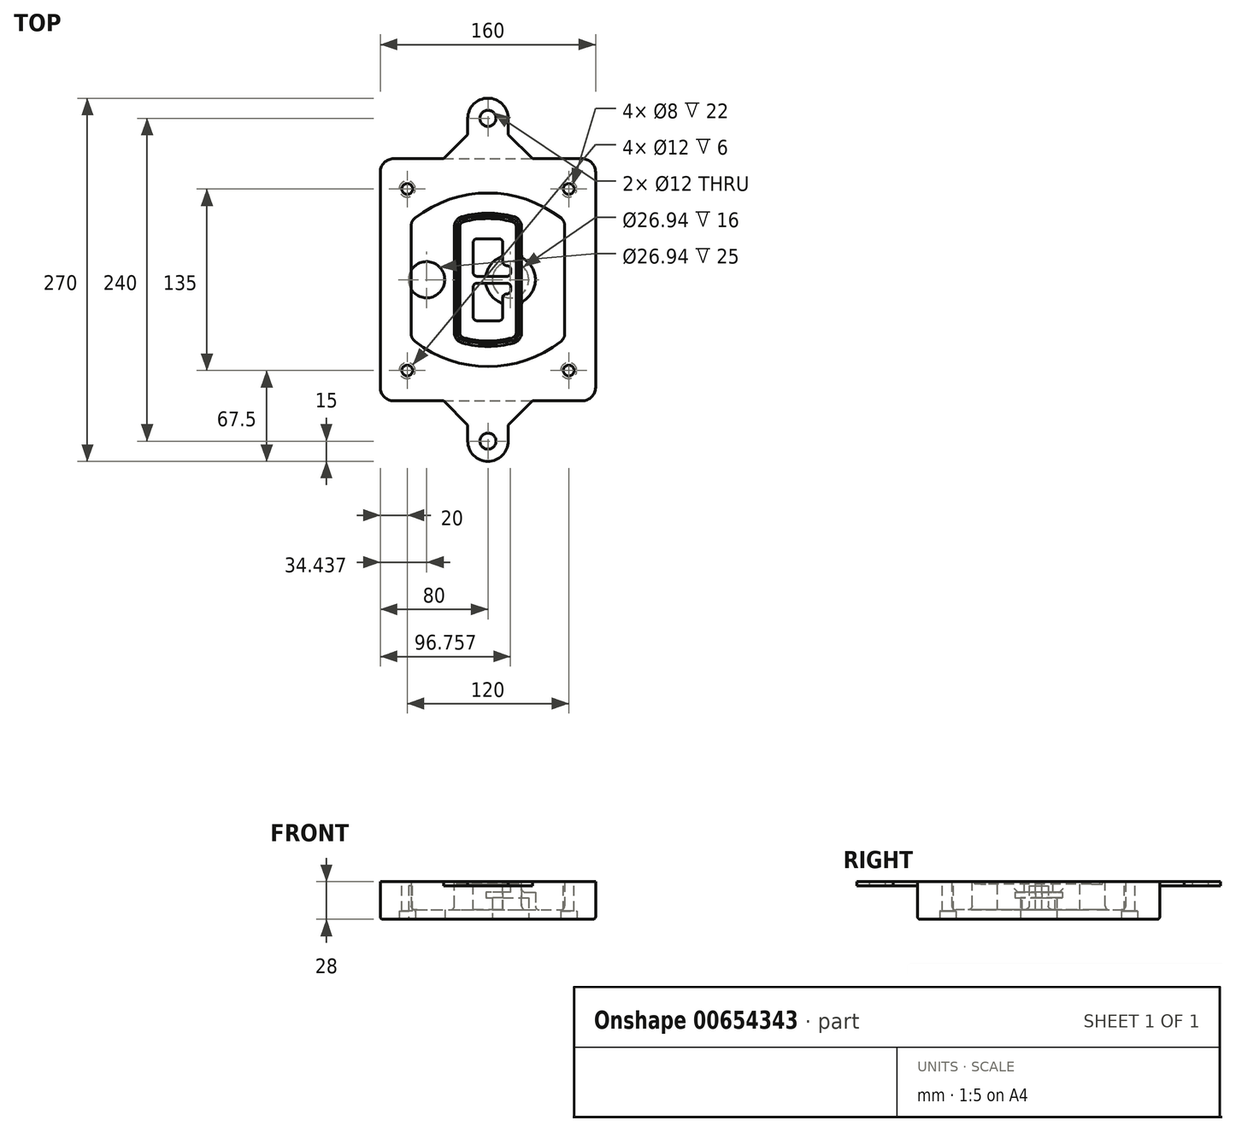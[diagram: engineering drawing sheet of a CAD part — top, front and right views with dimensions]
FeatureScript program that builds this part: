
annotation { "Feature Type Name" : "Feature", "Feature Type Description" : "" }
export const myFeature = defineFeature(function(context is Context, id is Id, definition is map)
    precondition{}
    {
        {
            var Q0;
            Q0=qCreatedBy(makeId("Top.planeOp"),FACE);
            var sketch = newSketch(context, id + "F0", { "sketchPlane" : qUnion([Q0])});
            skPoint(sketch, "E0.rect.middle", {"position": v(0, 0) * mm});
            skLineSegment(sketch, "E1.bottom", {"start": v(-70, -90) * mm, "end": v(70, -90) * mm});
            skLineSegment(sketch, "E1.top", {"start": v(-70, 90) * mm, "end": v(70, 90) * mm});
            skLineSegment(sketch, "E1.left", {"start": v(-80, -80) * mm, "end": v(-80, 80) * mm});
            skLineSegment(sketch, "E1.right", {"start": v(80, -80) * mm, "end": v(80, 80) * mm});
            skLineSegment(sketch, "E2", {"start": v(-80, 90) * mm, "end": v(80, -90) * mm, "construction": true});
            skLineSegment(sketch, "E3", {"start": v(80, 90) * mm, "end": v(-80, -90) * mm, "construction": true});
            skCircle(sketch, "E4", {"center": v(-60, 67.5) * mm, "radius": 4 * mm});
            skCircle(sketch, "E5", {"center": v(60, 67.5) * mm, "radius": 4 * mm});
            skCircle(sketch, "E6", {"center": v(60, -67.5) * mm, "radius": 4 * mm});
            skCircle(sketch, "E7", {"center": v(-60, -67.5) * mm, "radius": 4 * mm});
            skLineSegment(sketch, "E8", {"start": v(-60, 67.5) * mm, "end": v(60, 67.5) * mm, "construction": true});
            skLineSegment(sketch, "E9", {"start": v(60, 67.5) * mm, "end": v(60, -67.5) * mm, "construction": true});
            skLineSegment(sketch, "E10", {"start": v(60, -67.5) * mm, "end": v(-60, -67.5) * mm, "construction": true});
            skLineSegment(sketch, "E11", {"start": v(-60, -67.5) * mm, "end": v(-60, 67.5) * mm, "construction": true});
            skLineSegment(sketch, "E12", {"start": v(-60, 40.3) * mm, "end": v(-60, -40.3) * mm});
            skLineSegment(sketch, "E13", {"start": v(60, 40.3) * mm, "end": v(60, -40.3) * mm});
            skArc(sketch, "E14", {"start": v(56.15, 48.18) * mm, "mid": v(0, 67.5) * mm, "end": v(-56.15, 48.18) * mm});
            skArc(sketch, "E15", {"start": v(-56.15, -48.18) * mm, "mid": v(0, -67.5) * mm, "end": v(56.15, -48.18) * mm});
            skLineSegment(sketch, "E16", {"start": v(-60, 0) * mm, "end": v(60, 0) * mm, "construction": true});
            skPoint(sketch, "E17.visualSharp", {"position": v(-60, -45) * mm});
            skArc(sketch, "E17.filletArc", {"start": v(-60, -40.3) * mm, "mid": v(-58.99, -44.68) * mm, "end": v(-56.15, -48.18) * mm});
            skPoint(sketch, "E18.visualSharp", {"position": v(-60, 45) * mm});
            skArc(sketch, "E18.filletArc", {"start": v(-56.15, 48.18) * mm, "mid": v(-58.99, 44.68) * mm, "end": v(-60, 40.3) * mm});
            skPoint(sketch, "E19.visualSharp", {"position": v(60, 45) * mm});
            skArc(sketch, "E19.filletArc", {"start": v(60, 40.3) * mm, "mid": v(58.99, 44.68) * mm, "end": v(56.15, 48.18) * mm});
            skPoint(sketch, "E20.visualSharp", {"position": v(60, -45) * mm});
            skArc(sketch, "E20.filletArc", {"start": v(56.15, -48.18) * mm, "mid": v(58.99, -44.68) * mm, "end": v(60, -40.3) * mm});
            skPoint(sketch, "E21.visualSharp", {"position": v(-80, 90) * mm});
            skArc(sketch, "E21.filletArc", {"start": v(-70, 90) * mm, "mid": v(-77.07, 87.07) * mm, "end": v(-80, 80) * mm});
            skPoint(sketch, "E22.visualSharp", {"position": v(80, 90) * mm});
            skArc(sketch, "E22.filletArc", {"start": v(80, 80) * mm, "mid": v(77.07, 87.07) * mm, "end": v(70, 90) * mm});
            skPoint(sketch, "E23.visualSharp", {"position": v(80, -90) * mm});
            skArc(sketch, "E23.filletArc", {"start": v(70, -90) * mm, "mid": v(77.07, -87.07) * mm, "end": v(80, -80) * mm});
            skPoint(sketch, "E24.visualSharp", {"position": v(-80, -90) * mm});
            skArc(sketch, "E24.filletArc", {"start": v(-80, -80) * mm, "mid": v(-77.07, -87.07) * mm, "end": v(-70, -90) * mm});
            skArc(sketch, "E25.0", {"start": v(57, 40.3) * mm, "mid": v(56.3, 43.36) * mm, "end": v(54.3, 45.81) * mm});
            skLineSegment(sketch, "E25.1", {"start": v(57, 40.3) * mm, "end": v(57, -40.3) * mm});
            skArc(sketch, "E25.2", {"start": v(54.3, -45.81) * mm, "mid": v(56.3, -43.36) * mm, "end": v(57, -40.3) * mm});
            skArc(sketch, "E25.3", {"start": v(-54.3, -45.81) * mm, "mid": v(0, -64.5) * mm, "end": v(54.3, -45.81) * mm});
            skArc(sketch, "E25.4", {"start": v(-57, -40.3) * mm, "mid": v(-56.3, -43.36) * mm, "end": v(-54.3, -45.81) * mm});
            skArc(sketch, "E25.5", {"start": v(54.3, 45.81) * mm, "mid": v(0, 64.5) * mm, "end": v(-54.3, 45.81) * mm});
            skLineSegment(sketch, "E25.6", {"start": v(-57, 40.3) * mm, "end": v(-57, -40.3) * mm});
            skArc(sketch, "E25.7", {"start": v(-54.3, 45.81) * mm, "mid": v(-56.3, 43.36) * mm, "end": v(-57, 40.3) * mm});
            skArc(sketch, "E26.0", {"start": v(-58.62, 51.33) * mm, "mid": v(-62.58, 46.43) * mm, "end": v(-64, 40.3) * mm});
            skArc(sketch, "E26.1", {"start": v(58.62, 51.33) * mm, "mid": v(0, 71.5) * mm, "end": v(-58.62, 51.33) * mm});
            skArc(sketch, "E26.2", {"start": v(64, 40.3) * mm, "mid": v(62.58, 46.43) * mm, "end": v(58.62, 51.33) * mm});
            skLineSegment(sketch, "E26.3", {"start": v(64, 40.3) * mm, "end": v(64, -40.3) * mm});
            skArc(sketch, "E26.4", {"start": v(58.62, -51.33) * mm, "mid": v(62.58, -46.43) * mm, "end": v(64, -40.3) * mm});
            skLineSegment(sketch, "E26.5", {"start": v(-64, 40.3) * mm, "end": v(-64, -40.3) * mm});
            skArc(sketch, "E26.6", {"start": v(-58.62, -51.33) * mm, "mid": v(0, -71.5) * mm, "end": v(58.62, -51.33) * mm});
            skArc(sketch, "E26.7", {"start": v(-64, -40.3) * mm, "mid": v(-62.58, -46.43) * mm, "end": v(-58.62, -51.33) * mm});
            skSolve(sketch);
        }
        {
            var Q0;
            Q0=makeQuery(id+"F0.imprint","IMPRINT",FACE,{"disambiguationData":[TD([[makeQuery(id+"F0.imprint","IMPRINT",EDGE,{"derivedFrom":sQuery(id+"F0.wireOp",EDGE,"E1.bottom")}),1.0]])]});
            var Q1;
            Q1=makeQuery(id+"F0.imprint","IMPRINT",FACE,{"disambiguationData":[TD([[makeQuery(id+"F0.imprint","IMPRINT",EDGE,{"derivedFrom":sQuery(id+"F0.wireOp",EDGE,"E12")}),1.0]])]});
            var Q2;
            Q2=makeQuery(id+"F0.imprint","IMPRINT",FACE,{"disambiguationData":[TD([[makeQuery(id+"F0.imprint","IMPRINT",EDGE,{"derivedFrom":sQuery(id+"F0.wireOp",EDGE,"E25.0")}),1.0]])]});
            var Q3;
            Q3=makeQuery(id+"F0.imprint","IMPRINT",FACE,{"disambiguationData":[TD([[makeQuery(id+"F0.imprint","IMPRINT",EDGE,{"derivedFrom":sQuery(id+"F0.wireOp",EDGE,"E12")}),-1.0]])]});
            extrude(context, id + "F1", {"entities" : qUnion([Q0, Q1, Q2, Q3]), "oppositeDirection" : true, "depth" : 25 * mm});
        }
        {
            var Q0;
            Q0=makeQuery(id+"F0.imprint","IMPRINT",FACE,{"disambiguationData":[TD([[makeQuery(id+"F0.imprint","IMPRINT",EDGE,{"derivedFrom":sQuery(id+"F0.wireOp",EDGE,"E12")}),1.0]])]});
            extrude(context, id + "F2", {"entities" : qUnion([Q0]), "operationType" : NewBodyOperationType.ADD, "depth" : 3 * mm});
        }
        {
            var Q0;
            Q0=makeQuery(id+"F0.imprint","IMPRINT",FACE,{"disambiguationData":[TD([[makeQuery(id+"F0.imprint","IMPRINT",EDGE,{"derivedFrom":sQuery(id+"F0.wireOp",EDGE,"E25.0")}),1.0]])]});
            extrude(context, id + "F3", {"entities" : qUnion([Q0]), "operationType" : NewBodyOperationType.REMOVE, "oppositeDirection" : true, "depth" : 18 * mm});
        }
        {
            var Q0;
            Q0=makeQuery(id+"F2.opExtrude","CAP_FACE",FACE,{"disambiguationData":[OSD([sQuery(id+"F0.wireOp",EDGE,"E12"),sQuery(id+"F0.wireOp",EDGE,"E13"),sQuery(id+"F0.wireOp",EDGE,"E14"),sQuery(id+"F0.wireOp",EDGE,"E15"),sQuery(id+"F0.wireOp",EDGE,"E17.filletArc"),sQuery(id+"F0.wireOp",EDGE,"E18.filletArc"),sQuery(id+"F0.wireOp",EDGE,"E19.filletArc"),sQuery(id+"F0.wireOp",EDGE,"E20.filletArc"),sQuery(id+"F0.wireOp",EDGE,"E25.0"),sQuery(id+"F0.wireOp",EDGE,"E25.1"),sQuery(id+"F0.wireOp",EDGE,"E25.2"),sQuery(id+"F0.wireOp",EDGE,"E25.3"),sQuery(id+"F0.wireOp",EDGE,"E25.4"),sQuery(id+"F0.wireOp",EDGE,"E25.5"),sQuery(id+"F0.wireOp",EDGE,"E25.6"),sQuery(id+"F0.wireOp",EDGE,"E25.7")])],"isStart":false});
            var sketch = newSketch(context, id + "F4", { "sketchPlane" : qUnion([Q0])});
            skArc(sketch, "E27.0", {"start": v(-19.08, -46.97) * mm, "mid": v(0, -49.5) * mm, "end": v(19.08, -46.97) * mm});
            skArc(sketch, "E28.0", {"start": v(19.08, 46.97) * mm, "mid": v(0, 49.5) * mm, "end": v(-19.08, 46.97) * mm});
            skLineSegment(sketch, "E29", {"start": v(-25, 39.25) * mm, "end": v(-25, -39.25) * mm});
            skLineSegment(sketch, "E30", {"start": v(25, 39.25) * mm, "end": v(25, -39.25) * mm});
            skLineSegment(sketch, "E31", {"start": v(-25, 45.1) * mm, "end": v(25, 45.1) * mm, "construction": true});
            skLineSegment(sketch, "E32", {"start": v(-25, -45.1) * mm, "end": v(25, -45.1) * mm, "construction": true});
            skPoint(sketch, "E33.visualSharp", {"position": v(-25, 45.1) * mm});
            skArc(sketch, "E33.filletArc", {"start": v(-19.08, 46.97) * mm, "mid": v(-23.35, 44.11) * mm, "end": v(-25, 39.25) * mm});
            skPoint(sketch, "E34.visualSharp", {"position": v(25, 45.1) * mm});
            skArc(sketch, "E34.filletArc", {"start": v(25, 39.25) * mm, "mid": v(23.35, 44.11) * mm, "end": v(19.08, 46.97) * mm});
            skPoint(sketch, "E35.visualSharp", {"position": v(25, -45.1) * mm});
            skArc(sketch, "E35.filletArc", {"start": v(19.08, -46.97) * mm, "mid": v(23.35, -44.11) * mm, "end": v(25, -39.25) * mm});
            skPoint(sketch, "E36.visualSharp", {"position": v(-25, -45.1) * mm});
            skArc(sketch, "E36.filletArc", {"start": v(-25, -39.25) * mm, "mid": v(-23.35, -44.11) * mm, "end": v(-19.08, -46.97) * mm});
            skArc(sketch, "E37.0", {"start": v(54.3, 45.81) * mm, "mid": v(0, 64.5) * mm, "end": v(-54.3, 45.81) * mm});
            skArc(sketch, "E37.1", {"start": v(-54.3, 45.81) * mm, "mid": v(-56.3, 43.36) * mm, "end": v(-57, 40.3) * mm});
            skLineSegment(sketch, "E37.2", {"start": v(-57, 40.3) * mm, "end": v(-57, -40.3) * mm});
            skArc(sketch, "E37.3", {"start": v(-57, -40.3) * mm, "mid": v(-56.3, -43.36) * mm, "end": v(-54.3, -45.81) * mm});
            skArc(sketch, "E37.4", {"start": v(-54.3, -45.81) * mm, "mid": v(0, -64.5) * mm, "end": v(54.3, -45.81) * mm});
            skArc(sketch, "E37.5", {"start": v(54.3, -45.81) * mm, "mid": v(56.3, -43.36) * mm, "end": v(57, -40.3) * mm});
            skLineSegment(sketch, "E37.6", {"start": v(57, 40.3) * mm, "end": v(57, -40.3) * mm});
            skArc(sketch, "E37.7", {"start": v(57, 40.3) * mm, "mid": v(56.3, 43.36) * mm, "end": v(54.3, 45.81) * mm});
            skLineSegment(sketch, "E38.0", {"start": v(23, 39.25) * mm, "end": v(23, -39.25) * mm});
            skArc(sketch, "E38.1", {"start": v(18.56, -45.04) * mm, "mid": v(21.76, -42.9) * mm, "end": v(23, -39.25) * mm});
            skArc(sketch, "E38.2", {"start": v(-18.56, -45.04) * mm, "mid": v(0, -47.5) * mm, "end": v(18.56, -45.04) * mm});
            skArc(sketch, "E38.3", {"start": v(-23, -39.25) * mm, "mid": v(-21.76, -42.9) * mm, "end": v(-18.56, -45.04) * mm});
            skLineSegment(sketch, "E38.4", {"start": v(-23, 39.25) * mm, "end": v(-23, -39.25) * mm});
            skArc(sketch, "E38.5", {"start": v(23, 39.25) * mm, "mid": v(21.76, 42.9) * mm, "end": v(18.56, 45.04) * mm});
            skArc(sketch, "E38.6", {"start": v(-18.56, 45.04) * mm, "mid": v(-21.76, 42.9) * mm, "end": v(-23, 39.25) * mm});
            skArc(sketch, "E38.7", {"start": v(18.56, 45.04) * mm, "mid": v(0, 47.5) * mm, "end": v(-18.56, 45.04) * mm});
            skArc(sketch, "E39.0", {"start": v(21, 39.25) * mm, "mid": v(20.18, 41.68) * mm, "end": v(18.04, 43.1) * mm});
            skLineSegment(sketch, "E39.1", {"start": v(21, 39.25) * mm, "end": v(21, -39.25) * mm});
            skArc(sketch, "E39.2", {"start": v(18.04, -43.1) * mm, "mid": v(20.18, -41.68) * mm, "end": v(21, -39.25) * mm});
            skArc(sketch, "E39.3", {"start": v(-18.04, -43.1) * mm, "mid": v(0, -45.5) * mm, "end": v(18.04, -43.1) * mm});
            skArc(sketch, "E39.4", {"start": v(-21, -39.25) * mm, "mid": v(-20.18, -41.68) * mm, "end": v(-18.04, -43.1) * mm});
            skArc(sketch, "E39.5", {"start": v(18.04, 43.1) * mm, "mid": v(0, 45.5) * mm, "end": v(-18.04, 43.1) * mm});
            skLineSegment(sketch, "E39.6", {"start": v(-21, 39.25) * mm, "end": v(-21, -39.25) * mm});
            skArc(sketch, "E39.7", {"start": v(-18.04, 43.1) * mm, "mid": v(-20.18, 41.68) * mm, "end": v(-21, 39.25) * mm});
            skLineSegment(sketch, "E40", {"start": v(-25, 0) * mm, "end": v(25, 0) * mm, "construction": true});
            skLineSegment(sketch, "E41", {"start": v(-11, 5.5) * mm, "end": v(-11, 27.5) * mm});
            skLineSegment(sketch, "E42", {"start": v(-8, 30.5) * mm, "end": v(8, 30.5) * mm});
            skLineSegment(sketch, "E43", {"start": v(11, 27.5) * mm, "end": v(11, 13.5) * mm});
            skLineSegment(sketch, "E44", {"start": v(14, 10.5) * mm, "end": v(14, 10.5) * mm});
            skLineSegment(sketch, "E45", {"start": v(17, 7.5) * mm, "end": v(17, 5.5) * mm});
            skLineSegment(sketch, "E46", {"start": v(14, 2.5) * mm, "end": v(-8, 2.5) * mm});
            skPoint(sketch, "E47.visualSharp", {"position": v(-11, 30.5) * mm});
            skArc(sketch, "E47.filletArc", {"start": v(-8, 30.5) * mm, "mid": v(-10.12, 29.62) * mm, "end": v(-11, 27.5) * mm});
            skPoint(sketch, "E48.visualSharp", {"position": v(11, 30.5) * mm});
            skArc(sketch, "E48.filletArc", {"start": v(11, 27.5) * mm, "mid": v(10.12, 29.62) * mm, "end": v(8, 30.5) * mm});
            skPoint(sketch, "E49.visualSharp", {"position": v(11, 10.5) * mm});
            skArc(sketch, "E49.filletArc", {"start": v(11, 13.5) * mm, "mid": v(11.88, 11.38) * mm, "end": v(14, 10.5) * mm});
            skPoint(sketch, "E50.visualSharp", {"position": v(17, 10.5) * mm});
            skArc(sketch, "E50.filletArc", {"start": v(17, 7.5) * mm, "mid": v(16.12, 9.62) * mm, "end": v(14, 10.5) * mm});
            skPoint(sketch, "E51.visualSharp", {"position": v(17, 2.5) * mm});
            skArc(sketch, "E51.filletArc", {"start": v(14, 2.5) * mm, "mid": v(16.12, 3.38) * mm, "end": v(17, 5.5) * mm});
            skPoint(sketch, "E52.visualSharp", {"position": v(-11, 2.5) * mm});
            skArc(sketch, "E52.filletArc", {"start": v(-11, 5.5) * mm, "mid": v(-10.12, 3.38) * mm, "end": v(-8, 2.5) * mm});
            skLineSegment(sketch, "E53.0.MirrorCS", {"start": v(14, -2.5) * mm, "end": v(-8, -2.5) * mm});
            skArc(sketch, "E54.0.MirrorCS", {"start": v(-11, -5.5) * mm, "mid": v(-10.12, -3.38) * mm, "end": v(-8, -2.5) * mm});
            skLineSegment(sketch, "E55.0.MirrorCS", {"start": v(-11, -5.5) * mm, "end": v(-11, -27.5) * mm});
            skArc(sketch, "E56.0.MirrorCS", {"start": v(-8, -30.5) * mm, "mid": v(-10.12, -29.62) * mm, "end": v(-11, -27.5) * mm});
            skLineSegment(sketch, "E57.0.MirrorCS", {"start": v(-8, -30.5) * mm, "end": v(8, -30.5) * mm});
            skArc(sketch, "E58.0.MirrorCS", {"start": v(11, -27.5) * mm, "mid": v(10.12, -29.62) * mm, "end": v(8, -30.5) * mm});
            skLineSegment(sketch, "E59.0.MirrorCS", {"start": v(11, -27.5) * mm, "end": v(11, -13.5) * mm});
            skArc(sketch, "E60.0.MirrorCS", {"start": v(11, -13.5) * mm, "mid": v(11.88, -11.38) * mm, "end": v(14, -10.5) * mm});
            skArc(sketch, "E61.0.MirrorCS", {"start": v(17, -7.5) * mm, "mid": v(16.12, -9.62) * mm, "end": v(14, -10.5) * mm});
            skLineSegment(sketch, "E62.0.MirrorCS", {"start": v(17, -7.5) * mm, "end": v(17, -5.5) * mm});
            skArc(sketch, "E63.0.MirrorCS", {"start": v(14, -2.5) * mm, "mid": v(16.12, -3.38) * mm, "end": v(17, -5.5) * mm});
            skSolve(sketch);
        }
        {
            var Q0;
            Q0=makeQuery(id+"F4.imprint","IMPRINT",FACE,{"disambiguationData":[TD([[makeQuery(id+"F4.imprint","IMPRINT",EDGE,{"derivedFrom":sQuery(id+"F4.wireOp",EDGE,"E27.0")}),1.0]])]});
            var Q1;
            Q1=makeQuery(id+"F4.imprint","IMPRINT",FACE,{"disambiguationData":[TD([[makeQuery(id+"F4.imprint","IMPRINT",EDGE,{"derivedFrom":sQuery(id+"F4.wireOp",EDGE,"E38.0")}),-1.0]])]});
            var Q2;
            Q2=makeQuery(id+"F4.imprint","IMPRINT",FACE,{"disambiguationData":[TD([[makeQuery(id+"F4.imprint","IMPRINT",EDGE,{"derivedFrom":sQuery(id+"F4.wireOp",EDGE,"E39.0")}),1.0]])]});
            extrude(context, id + "F5", {"entities" : qUnion([Q0, Q1, Q2]), "operationType" : NewBodyOperationType.ADD, "endBound" : BoundingType.UP_TO_NEXT, "oppositeDirection" : true, "depth" : 25 * mm});
        }
        {
            var Q0;
            Q0=makeQuery(id+"F4.imprint","IMPRINT",FACE,{"disambiguationData":[TD([[makeQuery(id+"F4.imprint","IMPRINT",EDGE,{"derivedFrom":sQuery(id+"F4.wireOp",EDGE,"E38.0")}),-1.0]])]});
            extrude(context, id + "F6", {"entities" : qUnion([Q0]), "operationType" : NewBodyOperationType.REMOVE, "oppositeDirection" : true, "depth" : 2 * mm});
        }
        {
            var Q0;
            Q0=makeQuery(id+"F1.opExtrude","CAP_FACE",FACE,{"disambiguationData":[OSD([sQuery(id+"F0.wireOp",EDGE,"E1.bottom"),sQuery(id+"F0.wireOp",EDGE,"E1.top"),sQuery(id+"F0.wireOp",EDGE,"E1.left"),sQuery(id+"F0.wireOp",EDGE,"E1.right"),sQuery(id+"F0.wireOp",EDGE,"E4"),sQuery(id+"F0.wireOp",EDGE,"E5"),sQuery(id+"F0.wireOp",EDGE,"E6"),sQuery(id+"F0.wireOp",EDGE,"E7"),sQuery(id+"F0.wireOp",EDGE,"E21.filletArc"),sQuery(id+"F0.wireOp",EDGE,"E22.filletArc"),sQuery(id+"F0.wireOp",EDGE,"E23.filletArc"),sQuery(id+"F0.wireOp",EDGE,"E24.filletArc")])],"isStart":false});
            var sketch = newSketch(context, id + "F7", { "sketchPlane" : qUnion([Q0])});
            skCircle(sketch, "E64", {"center": v(16.76, 0) * mm, "radius": 13.47 * mm});
            skCircle(sketch, "E65", {"center": v(-45.56, 0) * mm, "radius": 13.47 * mm});
            skLineSegment(sketch, "E66", {"start": v(80, 0) * mm, "end": v(-80, 0) * mm});
            skCircle(sketch, "E67", {"center": v(16.76, 0) * mm, "radius": 18.47 * mm});
            skCircle(sketch, "E68", {"center": v(60, -67.5) * mm, "radius": 6 * mm});
            skCircle(sketch, "E69", {"center": v(-60, -67.5) * mm, "radius": 6 * mm});
            skCircle(sketch, "E70", {"center": v(-60, 67.5) * mm, "radius": 6 * mm});
            skCircle(sketch, "E71", {"center": v(60, 67.5) * mm, "radius": 6 * mm});
            skSolve(sketch);
        }
        {
            var Q0;
            {var subQ1=sQuery(id+"F7.wireOp",EDGE,"E66");var subQ4=sQuery(id+"F7.wireOp",EDGE,"E64");var subQ6=makeQuery(id+"F7.imprint","INTERSECT",VERTEX,{"disambiguationData":[OD(0.0)],"derivedFrom":[subQ4,subQ1]});Q0=makeQuery(id+"F7.imprint","IMPRINT",FACE,{"disambiguationData":[TD([[makeQuery(id+"F7.imprint","IMPRINT",EDGE,{"disambiguationData":[TD([[subQ6,-1.0]])],"derivedFrom":subQ4}),-1.0]])]});}
            var Q1;
            {var subQ0=sQuery(id+"F7.wireOp",EDGE,"E66");var subQ1=sQuery(id+"F7.wireOp",EDGE,"E64");var subQ3=makeQuery(id+"F7.imprint","INTERSECT",VERTEX,{"disambiguationData":[OD(0.0)],"derivedFrom":[subQ1,subQ0]});Q1=makeQuery(id+"F7.imprint","IMPRINT",FACE,{"disambiguationData":[TD([[makeQuery(id+"F7.imprint","IMPRINT",EDGE,{"disambiguationData":[TD([[subQ3,-1.0]])],"derivedFrom":subQ1}),1.0]])]});}
            var Q2;
            {var subQ0=sQuery(id+"F7.wireOp",EDGE,"E66");var subQ1=sQuery(id+"F7.wireOp",EDGE,"E64");var subQ3=makeQuery(id+"F7.imprint","INTERSECT",VERTEX,{"disambiguationData":[OD(0.0)],"derivedFrom":[subQ1,subQ0]});Q2=makeQuery(id+"F7.imprint","IMPRINT",FACE,{"disambiguationData":[TD([[makeQuery(id+"F7.imprint","IMPRINT",EDGE,{"disambiguationData":[TD([[subQ3,1.0]])],"derivedFrom":subQ1}),1.0]])]});}
            var Q3;
            {var subQ1=sQuery(id+"F7.wireOp",EDGE,"E66");var subQ4=sQuery(id+"F7.wireOp",EDGE,"E64");var subQ6=makeQuery(id+"F7.imprint","INTERSECT",VERTEX,{"disambiguationData":[OD(0.0)],"derivedFrom":[subQ4,subQ1]});Q3=makeQuery(id+"F7.imprint","IMPRINT",FACE,{"disambiguationData":[TD([[makeQuery(id+"F7.imprint","IMPRINT",EDGE,{"disambiguationData":[TD([[subQ6,1.0]])],"derivedFrom":subQ4}),-1.0]])]});}
            extrude(context, id + "F8", {"entities" : qUnion([Q0, Q1, Q2, Q3]), "operationType" : NewBodyOperationType.ADD, "oppositeDirection" : true, "depth" : 20 * mm});
        }
        {
            var Q0;
            {var subQ0=sQuery(id+"F7.wireOp",EDGE,"E66");var subQ1=sQuery(id+"F7.wireOp",EDGE,"E64");var subQ3=makeQuery(id+"F7.imprint","INTERSECT",VERTEX,{"disambiguationData":[OD(0.0)],"derivedFrom":[subQ1,subQ0]});Q0=makeQuery(id+"F7.imprint","IMPRINT",FACE,{"disambiguationData":[TD([[makeQuery(id+"F7.imprint","IMPRINT",EDGE,{"disambiguationData":[TD([[subQ3,-1.0]])],"derivedFrom":subQ1}),1.0]])]});}
            var Q1;
            {var subQ0=sQuery(id+"F7.wireOp",EDGE,"E66");var subQ1=sQuery(id+"F7.wireOp",EDGE,"E64");var subQ3=makeQuery(id+"F7.imprint","INTERSECT",VERTEX,{"disambiguationData":[OD(0.0)],"derivedFrom":[subQ1,subQ0]});Q1=makeQuery(id+"F7.imprint","IMPRINT",FACE,{"disambiguationData":[TD([[makeQuery(id+"F7.imprint","IMPRINT",EDGE,{"disambiguationData":[TD([[subQ3,1.0]])],"derivedFrom":subQ1}),1.0]])]});}
            extrude(context, id + "F9", {"entities" : qUnion([Q0, Q1]), "operationType" : NewBodyOperationType.REMOVE, "oppositeDirection" : true, "depth" : 16 * mm});
        }
        {
            var Q0;
            {var subQ0=sQuery(id+"F7.wireOp",EDGE,"E66");var subQ1=sQuery(id+"F7.wireOp",EDGE,"E65");var subQ3=makeQuery(id+"F7.imprint","INTERSECT",VERTEX,{"disambiguationData":[OD(0.0)],"derivedFrom":[subQ1,subQ0]});Q0=makeQuery(id+"F7.imprint","IMPRINT",FACE,{"disambiguationData":[TD([[makeQuery(id+"F7.imprint","IMPRINT",EDGE,{"disambiguationData":[TD([[subQ3,-1.0]])],"derivedFrom":subQ1}),1.0]])]});}
            var Q1;
            {var subQ0=sQuery(id+"F7.wireOp",EDGE,"E66");var subQ1=sQuery(id+"F7.wireOp",EDGE,"E65");var subQ3=makeQuery(id+"F7.imprint","INTERSECT",VERTEX,{"disambiguationData":[OD(0.0)],"derivedFrom":[subQ1,subQ0]});Q1=makeQuery(id+"F7.imprint","IMPRINT",FACE,{"disambiguationData":[TD([[makeQuery(id+"F7.imprint","IMPRINT",EDGE,{"disambiguationData":[TD([[subQ3,1.0]])],"derivedFrom":subQ1}),1.0]])]});}
            extrude(context, id + "F10", {"entities" : qUnion([Q0, Q1]), "operationType" : NewBodyOperationType.REMOVE, "oppositeDirection" : true, "depth" : 25 * mm});
        }
        {
            var Q0;
            Q0=makeQuery(id+"F7.imprint","IMPRINT",FACE,{"disambiguationData":[TD([[makeQuery(id+"F7.imprint","IMPRINT",EDGE,{"derivedFrom":sQuery(id+"F7.wireOp",EDGE,"E68")}),1.0]])]});
            var Q1;
            Q1=makeQuery(id+"F7.imprint","IMPRINT",FACE,{"disambiguationData":[TD([[makeQuery(id+"F7.imprint","IMPRINT",EDGE,{"derivedFrom":makeQuery(id+"F1.opExtrude","CAP_EDGE",EDGE,{"disambiguationData":[OSD([sQuery(id+"F0.wireOp",EDGE,"E5")])],"isStart":false})}),-1.0]])]});
            var Q2;
            Q2=makeQuery(id+"F7.imprint","IMPRINT",FACE,{"disambiguationData":[TD([[makeQuery(id+"F7.imprint","IMPRINT",EDGE,{"derivedFrom":sQuery(id+"F7.wireOp",EDGE,"E69")}),1.0]])]});
            var Q3;
            Q3=makeQuery(id+"F7.imprint","IMPRINT",FACE,{"disambiguationData":[TD([[makeQuery(id+"F7.imprint","IMPRINT",EDGE,{"derivedFrom":makeQuery(id+"F1.opExtrude","CAP_EDGE",EDGE,{"disambiguationData":[OSD([sQuery(id+"F0.wireOp",EDGE,"E4")])],"isStart":false})}),-1.0]])]});
            var Q4;
            Q4=makeQuery(id+"F7.imprint","IMPRINT",FACE,{"disambiguationData":[TD([[makeQuery(id+"F7.imprint","IMPRINT",EDGE,{"derivedFrom":sQuery(id+"F7.wireOp",EDGE,"E70")}),1.0]])]});
            var Q5;
            Q5=makeQuery(id+"F7.imprint","IMPRINT",FACE,{"disambiguationData":[TD([[makeQuery(id+"F7.imprint","IMPRINT",EDGE,{"derivedFrom":makeQuery(id+"F1.opExtrude","CAP_EDGE",EDGE,{"disambiguationData":[OSD([sQuery(id+"F0.wireOp",EDGE,"E7")])],"isStart":false})}),-1.0]])]});
            var Q6;
            Q6=makeQuery(id+"F7.imprint","IMPRINT",FACE,{"disambiguationData":[TD([[makeQuery(id+"F7.imprint","IMPRINT",EDGE,{"derivedFrom":sQuery(id+"F7.wireOp",EDGE,"E71")}),1.0]])]});
            var Q7;
            Q7=makeQuery(id+"F7.imprint","IMPRINT",FACE,{"disambiguationData":[TD([[makeQuery(id+"F7.imprint","IMPRINT",EDGE,{"derivedFrom":makeQuery(id+"F1.opExtrude","CAP_EDGE",EDGE,{"disambiguationData":[OSD([sQuery(id+"F0.wireOp",EDGE,"E6")])],"isStart":false})}),-1.0]])]});
            extrude(context, id + "F11", {"entities" : qUnion([Q0, Q1, Q2, Q3, Q4, Q5, Q6, Q7]), "operationType" : NewBodyOperationType.REMOVE, "oppositeDirection" : true, "depth" : 6 * mm});
        }
        {
            var Q0;
            Q0=makeQuery(id+"F9.boolean.opBoolean","COPY",FACE,{"derivedFrom":makeQuery(id+"F9.opExtrude","CAP_FACE",FACE,{"disambiguationData":[OSD([sQuery(id+"F7.wireOp",EDGE,"E64")])],"isStart":false})});
            var sketch = newSketch(context, id + "F12", { "sketchPlane" : qUnion([Q0])});
            skArc(sketch, "E72.0", {"start": v(11, 17.55) * mm, "mid": v(2.57, 11.82) * mm, "end": v(-1.54, 2.5) * mm});
            skArc(sketch, "E72.1", {"start": v(-1.54, -2.5) * mm, "mid": v(2.57, -11.82) * mm, "end": v(11, -17.55) * mm});
            skLineSegment(sketch, "E73", {"start": v(-1.54, -2.5) * mm, "end": v(14, -2.5) * mm});
            skLineSegment(sketch, "E74.0", {"start": v(14, 2.5) * mm, "end": v(-1.54, 2.5) * mm});
            skArc(sketch, "E74.1", {"start": v(14, 2.5) * mm, "mid": v(16.12, 3.38) * mm, "end": v(17, 5.5) * mm});
            skLineSegment(sketch, "E74.2", {"start": v(17, 7.5) * mm, "end": v(17, 5.5) * mm});
            skArc(sketch, "E74.3", {"start": v(17, 7.5) * mm, "mid": v(16.12, 9.62) * mm, "end": v(14, 10.5) * mm});
            skArc(sketch, "E74.4", {"start": v(11, 13.5) * mm, "mid": v(11.88, 11.38) * mm, "end": v(14, 10.5) * mm});
            skLineSegment(sketch, "E74.5", {"start": v(11, 17.55) * mm, "end": v(11, 13.5) * mm});
            skLineSegment(sketch, "E74.7", {"start": v(14, -2.5) * mm, "end": v(-1.54, -2.5) * mm});
            skArc(sketch, "E74.8", {"start": v(14, -2.5) * mm, "mid": v(16.12, -3.38) * mm, "end": v(17, -5.5) * mm});
            skLineSegment(sketch, "E74.9", {"start": v(17, -7.5) * mm, "end": v(17, -5.5) * mm});
            skArc(sketch, "E74.10", {"start": v(17, -7.5) * mm, "mid": v(16.12, -9.62) * mm, "end": v(14, -10.5) * mm});
            skArc(sketch, "E74.11", {"start": v(11, -13.5) * mm, "mid": v(11.88, -11.38) * mm, "end": v(14, -10.5) * mm});
            skLineSegment(sketch, "E74.12", {"start": v(11, -17.55) * mm, "end": v(11, -13.5) * mm});
            skPoint(sketch, "E75.orphan", {"position": v(11, -27.5) * mm});
            skPoint(sketch, "E76.orphan", {"position": v(-8, -2.5) * mm});
            skPoint(sketch, "E77.orphan", {"position": v(-8, 2.5) * mm});
            skPoint(sketch, "E78.orphan", {"position": v(11, 27.5) * mm});
            skSolve(sketch);
        }
        {
            var Q0;
            {var subQ7=sQuery(id+"F12.wireOp",EDGE,"E72.0");var subQ14=sQuery(id+"F12.wireOp",EDGE,"E72.1");var subQ16=sQuery(id+"F12.wireOp",EDGE,"E74.1");var subQ18=sQuery(id+"F12.wireOp",EDGE,"E74.8");Q0=qUnion([makeQuery(id+"F12.imprint","IMPRINT",FACE,{"disambiguationData":[TD([[makeQuery(id+"F12.imprint","IMPRINT",EDGE,{"derivedFrom":subQ7}),1.0]])]}),makeQuery(id+"F12.imprint","IMPRINT",FACE,{"disambiguationData":[TD([[makeQuery(id+"F12.imprint","IMPRINT",EDGE,{"derivedFrom":subQ14}),1.0]])]}),makeQuery(id+"F12.imprint","IMPRINT",FACE,{"disambiguationData":[TD([[makeQuery(id+"F12.imprint","IMPRINT",EDGE,{"derivedFrom":subQ16}),1.0]])]}),makeQuery(id+"F12.imprint","IMPRINT",FACE,{"disambiguationData":[TD([[makeQuery(id+"F12.imprint","IMPRINT",EDGE,{"derivedFrom":subQ18}),-1.0]])]})]);}
            var Q1;
            Q1=makeQuery(id+"F5.boolean.opBoolean","SPLIT",FACE,{"disambiguationData":[TD([makeQuery(id+"F5.opExtrude","SWEPT_FACE",FACE,{"disambiguationData":[OSD([sQuery(id+"F4.wireOp",EDGE,"E41")])]})])],"derivedFrom":makeQuery(id+"F3.boolean.opBoolean","COPY",FACE,{"derivedFrom":makeQuery(id+"F3.opExtrude","CAP_FACE",FACE,{"disambiguationData":[OSD([sQuery(id+"F0.wireOp",EDGE,"E25.0"),sQuery(id+"F0.wireOp",EDGE,"E25.1"),sQuery(id+"F0.wireOp",EDGE,"E25.2"),sQuery(id+"F0.wireOp",EDGE,"E25.3"),sQuery(id+"F0.wireOp",EDGE,"E25.4"),sQuery(id+"F0.wireOp",EDGE,"E25.5"),sQuery(id+"F0.wireOp",EDGE,"E25.6"),sQuery(id+"F0.wireOp",EDGE,"E25.7")])],"isStart":false})})});
            extrude(context, id + "F13", {"entities" : qUnion([Q0]), "operationType" : NewBodyOperationType.REMOVE, "endBound" : BoundingType.UP_TO_SURFACE, "endBoundEntityFace" : qUnion([Q1]), "depth" : 25 * mm});
        }
        {
            var Q0;
            Q0=makeQuery(id+"F3.boolean.opBoolean","COPY",EDGE,{"derivedFrom":makeQuery(id+"F3.opExtrude","CAP_EDGE",EDGE,{"disambiguationData":[OSD([sQuery(id+"F0.wireOp",EDGE,"E25.6")])],"isStart":false})});
            var Q1;
            Q1=makeQuery(id+"F8.boolean.opBoolean","INTERSECT",EDGE,{"derivedFrom":[makeQuery(id+"F5.opExtrude","SWEPT_FACE",FACE,{"disambiguationData":[OSD([sQuery(id+"F4.wireOp",EDGE,"E30")])]}),makeQuery(id+"F8.opExtrude","CAP_FACE",FACE,{"disambiguationData":[OSD([sQuery(id+"F7.wireOp",EDGE,"E67")])],"isStart":false})]});
            var Q2;
            Q2=makeQuery(id+"F8.boolean.opBoolean","INTERSECT",EDGE,{"disambiguationData":[OD(1.0)],"derivedFrom":[makeQuery(id+"F5.opExtrude","SWEPT_FACE",FACE,{"disambiguationData":[OSD([sQuery(id+"F4.wireOp",EDGE,"E30")])]}),makeQuery(id+"F8.opExtrude","SWEPT_FACE",FACE,{"disambiguationData":[OSD([sQuery(id+"F7.wireOp",EDGE,"E67")])]})]});
            var Q3;
            {var subQ0=sQuery(id+"F4.wireOp",EDGE,"E30");Q3=makeQuery(id+"F8.boolean.opBoolean","SPLIT",EDGE,{"disambiguationData":[TD([makeQuery(id+"F5.opExtrude","SWEPT_FACE",FACE,{"disambiguationData":[OSD([sQuery(id+"F4.wireOp",EDGE,"E35.filletArc")])]})])],"derivedFrom":makeQuery(id+"F5.opExtrude","CAP_EDGE",EDGE,{"disambiguationData":[OSD([subQ0])],"isStart":false})});}
            var Q4;
            {var subQ0=sQuery(id+"F0.wireOp",EDGE,"E25.7");var subQ1=sQuery(id+"F0.wireOp",EDGE,"E25.1");var subQ2=sQuery(id+"F0.wireOp",EDGE,"E25.6");var subQ3=sQuery(id+"F0.wireOp",EDGE,"E25.5");var subQ4=sQuery(id+"F0.wireOp",EDGE,"E25.4");var subQ5=sQuery(id+"F0.wireOp",EDGE,"E25.0");var subQ6=sQuery(id+"F0.wireOp",EDGE,"E25.2");var subQ7=sQuery(id+"F0.wireOp",EDGE,"E25.3");Q4=makeQuery(id+"F8.boolean.opBoolean","INTERSECT",EDGE,{"derivedFrom":[makeQuery(id+"F5.boolean.opBoolean","SPLIT",FACE,{"disambiguationData":[TD([makeQuery(id+"F2.opExtrude","SWEPT_FACE",FACE,{"disambiguationData":[OSD([subQ5])]})])],"derivedFrom":makeQuery(id+"F3.boolean.opBoolean","COPY",FACE,{"derivedFrom":makeQuery(id+"F3.opExtrude","CAP_FACE",FACE,{"disambiguationData":[OSD([subQ5,subQ1,subQ6,subQ7,subQ4,subQ3,subQ2,subQ0])],"isStart":false})})}),makeQuery(id+"F8.opExtrude","SWEPT_FACE",FACE,{"disambiguationData":[OSD([sQuery(id+"F7.wireOp",EDGE,"E67")])]})]});}
            var Q5;
            Q5=makeQuery(id+"F8.boolean.opBoolean","INTERSECT",EDGE,{"disambiguationData":[OD(0.0)],"derivedFrom":[makeQuery(id+"F5.opExtrude","SWEPT_FACE",FACE,{"disambiguationData":[OSD([sQuery(id+"F4.wireOp",EDGE,"E30")])]}),makeQuery(id+"F8.opExtrude","SWEPT_FACE",FACE,{"disambiguationData":[OSD([sQuery(id+"F7.wireOp",EDGE,"E67")])]})]});
            fillet(context, id + "F14", {"entities" : qUnion([Q0, Q1, Q2, Q3, Q4, Q5]), "radius" : 3 * mm, "tangentPropagation" : true, "allowEdgeOverflow" : false});
        }
        {
            var Q0;
            Q0=makeQuery(id+"F1.opExtrude","CAP_EDGE",EDGE,{"disambiguationData":[OSD([sQuery(id+"F0.wireOp",EDGE,"E1.bottom")])],"isStart":false});
            fillet(context, id + "F15", {"entities" : qUnion([Q0]), "radius" : 2 * mm, "tangentPropagation" : true, "allowEdgeOverflow" : false});
        }
        {
            var Q0;
            {var subQ0=sQuery(id+"F0.wireOp",EDGE,"E21.filletArc");var subQ1=sQuery(id+"F0.wireOp",EDGE,"E7");var subQ2=sQuery(id+"F0.wireOp",EDGE,"E6");var subQ3=sQuery(id+"F0.wireOp",EDGE,"E5");var subQ4=sQuery(id+"F0.wireOp",EDGE,"E4");var subQ5=sQuery(id+"F0.wireOp",EDGE,"E22.filletArc");var subQ6=sQuery(id+"F0.wireOp",EDGE,"E1.bottom");var subQ7=sQuery(id+"F0.wireOp",EDGE,"E1.right");var subQ8=sQuery(id+"F0.wireOp",EDGE,"E1.top");var subQ9=sQuery(id+"F0.wireOp",EDGE,"E1.left");var subQ10=sQuery(id+"F0.wireOp",EDGE,"E23.filletArc");var subQ11=sQuery(id+"F0.wireOp",EDGE,"E24.filletArc");Q0=makeQuery(id+"F2.boolean.opBoolean","SPLIT",FACE,{"disambiguationData":[TD([makeQuery(id+"F1.opExtrude","SWEPT_FACE",FACE,{"disambiguationData":[OSD([subQ6])]})])],"derivedFrom":makeQuery(id+"F1.opExtrude","CAP_FACE",FACE,{"disambiguationData":[OSD([subQ6,subQ8,subQ9,subQ7,subQ4,subQ3,subQ2,subQ1,subQ0,subQ5,subQ10,subQ11])],"isStart":true})});}
            var sketch = newSketch(context, id + "F16", { "sketchPlane" : qUnion([Q0])});
            skLineSegment(sketch, "E79", {"start": v(-33, 90) * mm, "end": v(-15, 108) * mm});
            skLineSegment(sketch, "E80", {"start": v(-15, 108) * mm, "end": v(-15, 120) * mm});
            skLineSegment(sketch, "E81", {"start": v(0, 90) * mm, "end": v(0, 120) * mm, "construction": true});
            skCircle(sketch, "E82", {"center": v(0, 120) * mm, "radius": 6 * mm});
            skLineSegment(sketch, "E83", {"start": v(15, 120) * mm, "end": v(15, 108) * mm});
            skLineSegment(sketch, "E84", {"start": v(15, 108) * mm, "end": v(33, 90) * mm});
            skArc(sketch, "E85", {"start": v(-15, 120) * mm, "mid": v(0, 135) * mm, "end": v(15, 120) * mm});
            skLineSegment(sketch, "E86", {"start": v(-80, 0) * mm, "end": v(80, 0) * mm, "construction": true});
            skLineSegment(sketch, "E87.MirrorCS", {"start": v(-33, -90) * mm, "end": v(-15, -108) * mm});
            skLineSegment(sketch, "E88.MirrorCS", {"start": v(-15, -108) * mm, "end": v(-15, -120) * mm});
            skArc(sketch, "E89.MirrorCS", {"start": v(-15, -120) * mm, "mid": v(0, -135) * mm, "end": v(15, -120) * mm});
            skLineSegment(sketch, "E90.MirrorCS", {"start": v(15, -120) * mm, "end": v(15, -108) * mm});
            skLineSegment(sketch, "E91.MirrorCS", {"start": v(15, -108) * mm, "end": v(33, -90) * mm});
            skLineSegment(sketch, "E92.MirrorCS", {"start": v(0, -90) * mm, "end": v(0, -120) * mm, "construction": true});
            skCircle(sketch, "E93.MirrorC", {"center": v(0, -120) * mm, "radius": 6 * mm});
            skSolve(sketch);
        }
        {
            var Q0;
            Q0=makeQuery(id+"F16.imprint","IMPRINT",FACE,{"disambiguationData":[TD([[makeQuery(id+"F16.imprint","IMPRINT",EDGE,{"derivedFrom":makeQuery(id+"F1.opExtrude","CAP_EDGE",EDGE,{"disambiguationData":[OSD([sQuery(id+"F0.wireOp",EDGE,"E1.left")])],"isStart":true})}),-1.0]])]});
            var Q1;
            {var subQ0=sQuery(id+"F16.wireOp",EDGE,"E79");Q1=makeQuery(id+"F16.imprint","IMPRINT",FACE,{"disambiguationData":[TD([[makeQuery(id+"F16.imprint","IMPRINT",EDGE,{"derivedFrom":subQ0}),-1.0]])]});}
            var Q2;
            {var subQ0=sQuery(id+"F16.wireOp",EDGE,"E87.MirrorCS");Q2=makeQuery(id+"F16.imprint","IMPRINT",FACE,{"disambiguationData":[TD([[makeQuery(id+"F16.imprint","IMPRINT",EDGE,{"derivedFrom":subQ0}),1.0]])]});}
            var Q3;
            Q3=makeQuery(id+"F2.opExtrude","CAP_FACE",FACE,{"disambiguationData":[OSD([sQuery(id+"F0.wireOp",EDGE,"E12"),sQuery(id+"F0.wireOp",EDGE,"E13"),sQuery(id+"F0.wireOp",EDGE,"E14"),sQuery(id+"F0.wireOp",EDGE,"E15"),sQuery(id+"F0.wireOp",EDGE,"E17.filletArc"),sQuery(id+"F0.wireOp",EDGE,"E18.filletArc"),sQuery(id+"F0.wireOp",EDGE,"E19.filletArc"),sQuery(id+"F0.wireOp",EDGE,"E20.filletArc"),sQuery(id+"F0.wireOp",EDGE,"E25.0"),sQuery(id+"F0.wireOp",EDGE,"E25.1"),sQuery(id+"F0.wireOp",EDGE,"E25.2"),sQuery(id+"F0.wireOp",EDGE,"E25.3"),sQuery(id+"F0.wireOp",EDGE,"E25.4"),sQuery(id+"F0.wireOp",EDGE,"E25.5"),sQuery(id+"F0.wireOp",EDGE,"E25.6"),sQuery(id+"F0.wireOp",EDGE,"E25.7")])],"isStart":false});
            extrude(context, id + "F17", {"entities" : qUnion([Q0, Q1, Q2]), "operationType" : NewBodyOperationType.ADD, "endBound" : BoundingType.UP_TO_SURFACE, "depth" : 25 * mm, "endBoundEntityFace" : qUnion([Q3]), "offsetDistance" : 25 * mm});
        }
    });
